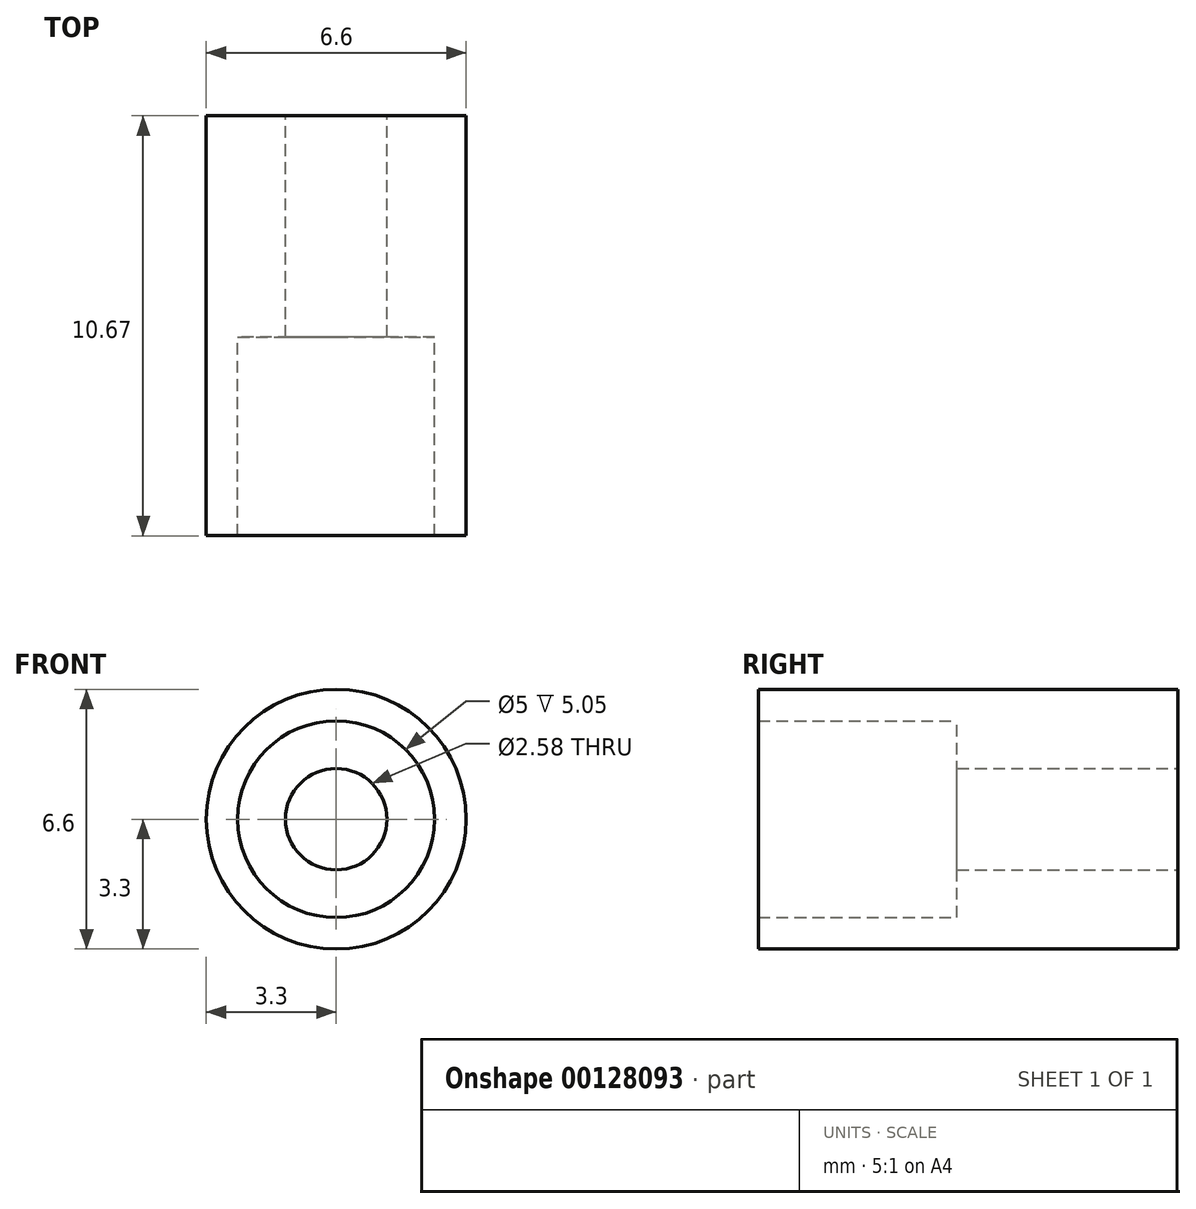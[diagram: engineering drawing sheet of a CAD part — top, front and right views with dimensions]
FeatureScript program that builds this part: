
annotation { "Feature Type Name" : "Feature", "Feature Type Description" : "" }
export const myFeature = defineFeature(function(context is Context, id is Id, definition is map)
    precondition{}
    {
        {
            var Q0;
            Q0=qCreatedBy(makeId("Front.planeOp"),FACE);
            var sketch = newSketch(context, id + "F0", { "sketchPlane" : qUnion([Q0])});
            skCircle(sketch, "E0", {"center": v(0, 0) * mm, "radius": 2.5 * mm});
            skCircle(sketch, "E1", {"center": v(0, 0) * mm, "radius": 3.3 * mm});
            skSolve(sketch);
        }
        {
            var Q0;
            Q0=makeQuery(id+"F0.imprint","IMPRINT",FACE,{"disambiguationData":[TD([[makeQuery(id+"F0.imprint","IMPRINT",EDGE,{"derivedFrom":sQuery(id+"F0.wireOp",EDGE,"E0")}),-1.0]])]});
            extrude(context, id + "F1", {"entities" : qUnion([Q0]), "depth" : 10.67 * mm});
        }
        {
            var Q0;
            Q0=qCreatedBy(makeId("Front.planeOp"),FACE);
            var sketch = newSketch(context, id + "F2", { "sketchPlane" : qUnion([Q0])});
            skCircle(sketch, "E2", {"center": v(0, 0) * mm, "radius": 1.29 * mm});
            skCircle(sketch, "E3", {"center": v(0, 0) * mm, "radius": 2.52 * mm});
            skSolve(sketch);
        }
        {
            var Q0;
            Q0=makeQuery(id+"F2.imprint","IMPRINT",FACE,{"disambiguationData":[TD([[makeQuery(id+"F2.imprint","IMPRINT",EDGE,{"derivedFrom":sQuery(id+"F2.wireOp",EDGE,"E2")}),-1.0]])]});
            extrude(context, id + "F3", {"entities" : qUnion([Q0]), "operationType" : NewBodyOperationType.ADD, "depth" : 5.62 * mm});
        }
    });
